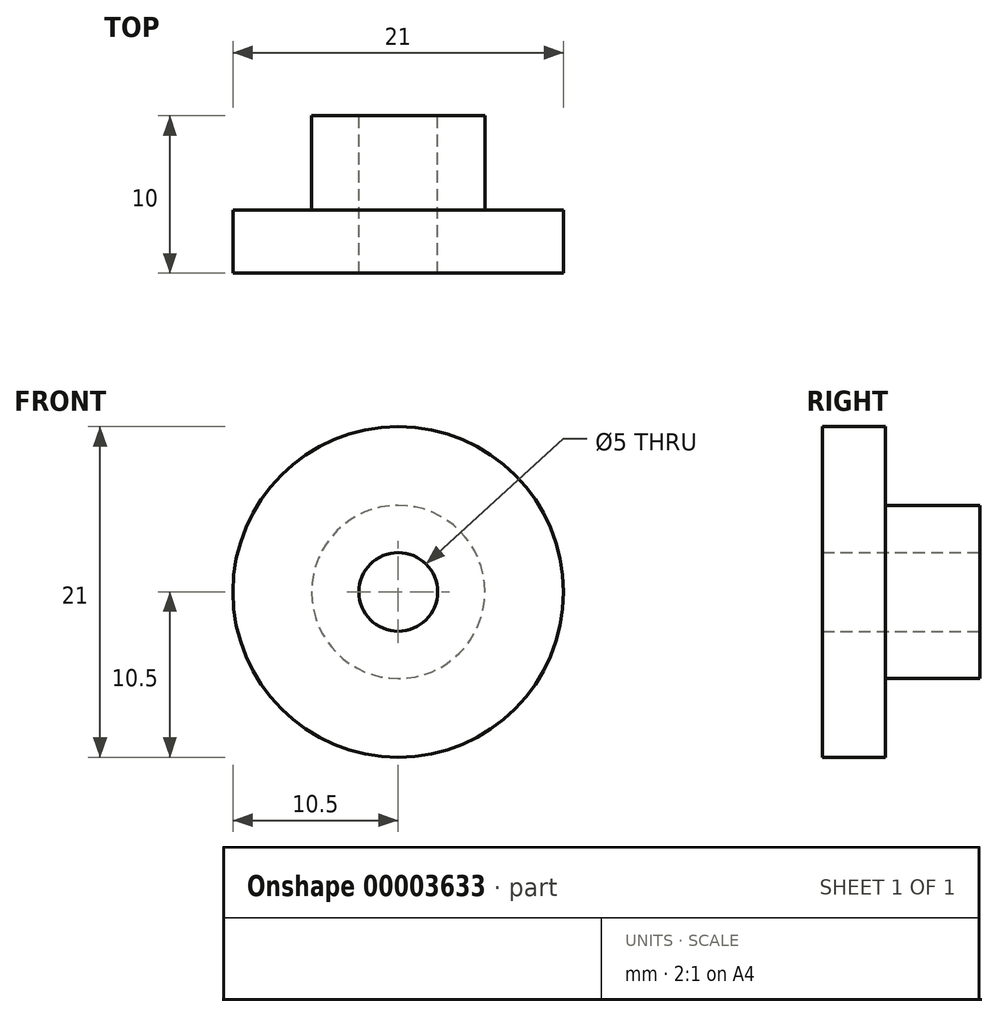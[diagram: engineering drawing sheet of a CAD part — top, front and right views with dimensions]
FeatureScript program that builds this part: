
annotation { "Feature Type Name" : "Feature", "Feature Type Description" : "" }
export const myFeature = defineFeature(function(context is Context, id is Id, definition is map)
    precondition{}
    {
        {
            var Q0;
            Q0=qCreatedBy(makeId("Front.planeOp"),FACE);
            var sketch = newSketch(context, id + "F0", { "sketchPlane" : qUnion([Q0])});
            skCircle(sketch, "E0", {"center": v(0, 0) * mm, "radius": 10.5 * mm});
            skCircle(sketch, "E1", {"center": v(0, 0) * mm, "radius": 5.5 * mm});
            skSolve(sketch);
        }
        {
            var Q0;
            Q0=makeQuery(id+"F0.imprint","IMPRINT",FACE,{"disambiguationData":[TD([[makeQuery(id+"F0.imprint","IMPRINT",EDGE,{"derivedFrom":sQuery(id+"F0.wireOp",EDGE,"E1")}),1.0]])]});
            extrude(context, id + "F1", {"entities" : qUnion([Q0]), "oppositeDirection" : true, "depth" : 10 * mm});
        }
        {
            var Q0;
            Q0=makeQuery(id+"F1.opExtrude","CAP_FACE",FACE,{"disambiguationData":[OSD([sQuery(id+"F0.wireOp",EDGE,"E1"),sQuery(id+"F0.wireOp",EDGE,"39ac3ea4-6015-4e25-92df-9d38e0707735")])],"isStart":true});
            var Q1;
            Q1=makeQuery(id+"F0.imprint","IMPRINT",FACE,{"disambiguationData":[TD([[makeQuery(id+"F0.imprint","IMPRINT",EDGE,{"derivedFrom":sQuery(id+"F0.wireOp",EDGE,"E0")}),1.0]])]});
            extrude(context, id + "F2", {"entities" : qUnion([Q0, Q1]), "operationType" : NewBodyOperationType.ADD, "oppositeDirection" : true, "depth" : 4 * mm});
        }
        {
            var Q0;
            Q0=sQuery(id+"F0.wireOp",VERTEX,"E0.center");
            var Q1;
            Q1=makeQuery(id+"F1.opExtrude","SWEPT_BODY",BODY,{"disambiguationData":[OSD([sQuery(id+"F0.wireOp",EDGE,"E1")])]});
            hole(context, id + "F3", {"style" : HoleStyle.SIMPLE, "endStyle" : HoleEndStyle.THROUGH, "standardTappedOrClearance" : lookupTablePath({ "standard" : "ISO", "size" : "5", "type" : "Drilled" }), "standardBlindInLast" : lookupTablePath({ "standard" : "ISO", "size" : "5", "type" : "Drilled" }), "holeDiameter" : 5 * mm, "tappedDepth" : 12 * mm, "tapClearance" : 3, "locations" : qUnion([Q0]), "scope" : qUnion([Q1]), "startStyle" : HoleStartStyle.SKETCH});
        }
    });
